# Revit family: Water_Heater-Rinnai-Ultra-Condensing-Tankless-RUR98i
name_source: partatom
category: Mechanical Equipment
revit_build: Autodesk Revit MEP 2012 (Build: 20110916_2132(x64)
units: mm (PartAtom-declared; Revit-internal decimal feet)

## types (1)
- Standard
    Applicable Altitude Range = 0-10,200ft (0-3,109m)
    Cap = Metal - Rinnai - Aluminum - Polished Sliver
    Clearance for Front = 6"
    Clearance for Ground or Bottom = 12"
    Clearance for Sides = 2"
    Clearance for Top = 6"
    Cold Water Connection = Cold Water Connector
    Combustibles = Yes
    Combustion Air = Indoor
    Default Elevation = 48"
    Depth = 10"
    Description = Tankless Water Heater
    Dry Weight = 72.80 lb
    Electrical Consumption Range = Normal: 205 w, Standby: 3 w
    Frequency = 60 Hz
    Gas Connection = Gas Connector
    Gas Input Range = 15,200 - 199,000 BTU/h
    Gas Input Rate = 199.0 Btu/h
    Gas Manifold Pressure High Fire = 3" (NG); 3.5" (Propane)
    Gas Manifold Pressure Low Fire = .42" (NG); .47" (Propane)
    Gas Supply Pressure Max = 10.5" (NG); 13.5" (Propane)
    Gas Supply Pressure Min = 4" (NG); 8" (Propane)
    Height = 26"
    Hot Water Connection = Hot Water Connector
    Ignition System = Direct electronic ignition
    Installation Location = Indoor only
    Installation URL = https://www.rinnai.us
    Interference = Glass - Rinnai - Clear - Amber
    Liquid Propane = Yes
    Manufacturer = Rinnai America Corporation
    Manufacturer Fax = 678-829-1666
    Max Amperage = 8 A
    Model = REU-KBP3237FFUD-US
    Natural Gas = Yes
    Panel = Metal - Rinnai - Aluminum Frame - Painted White
    Product Page URL = https://rinnai.us
    Spec Sheet URL = https://www.rinnai.us
    Subcategory = Tankless Water Heaters
    Temperature Settings = 98° - 140° F
    URL = https://rinnai.us
    Unit = Metal - Rinnai - Aluminum Frame - Painted White
    Venting = Direct Vent system 3-4" configurations
    Voltage = 120 V
    Warranty URL = https://www.rinnai.us
    Wattage = 205 W
    Width = 18 1/2"

## geometry (parser evidence)
native form markers: Blend x2, Sweep x9
no freeform markers — native parametric forms only
